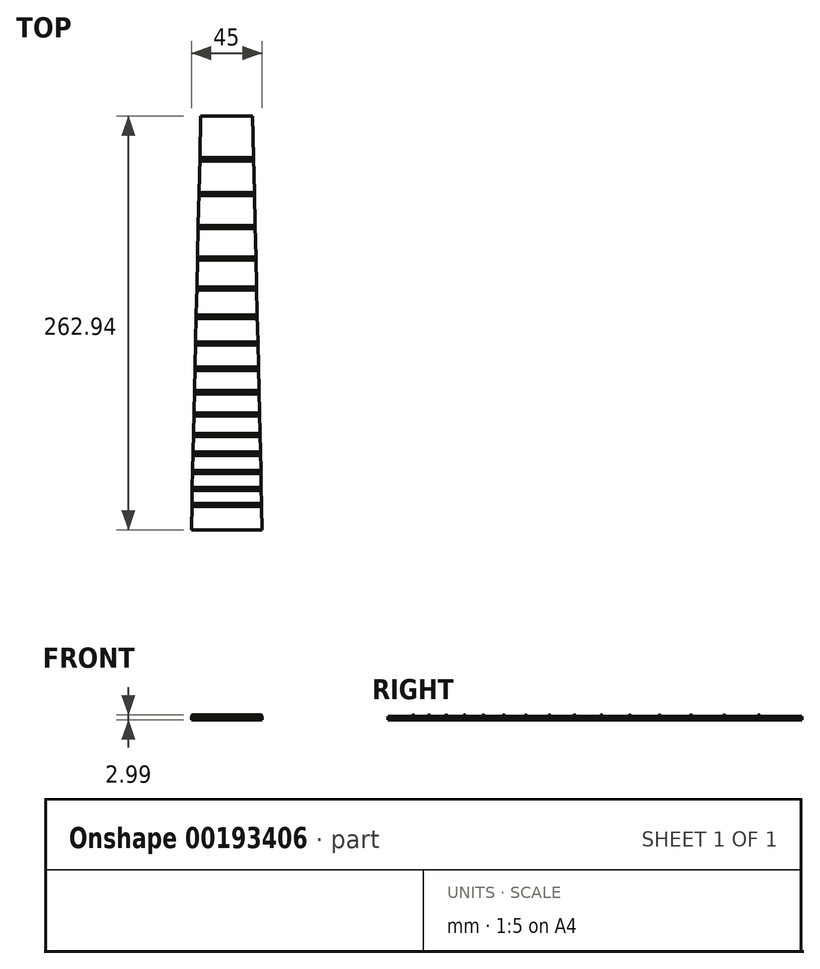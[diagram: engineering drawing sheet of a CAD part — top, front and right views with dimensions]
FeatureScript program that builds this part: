
annotation { "Feature Type Name" : "Feature", "Feature Type Description" : "" }
export const myFeature = defineFeature(function(context is Context, id is Id, definition is map)
    precondition{}
    {
        {
            var Q0;
            Q0=qCreatedBy(makeId("Top.planeOp"),FACE);
            var sketch = newSketch(context, id + "F0", { "sketchPlane" : qUnion([Q0])});
            skLineSegment(sketch, "E0", {"start": v(-15.06, 218.37) * mm, "end": v(17.94, 218.37) * mm});
            skLineSegment(sketch, "E1", {"start": v(17.94, 218.37) * mm, "end": v(23.94, -44.57) * mm});
            skLineSegment(sketch, "E2", {"start": v(23.94, -44.57) * mm, "end": v(-21.06, -44.57) * mm});
            skLineSegment(sketch, "E3", {"start": v(-21.06, -44.57) * mm, "end": v(-15.06, 218.37) * mm});
            skSolve(sketch);
        }
        {
            var Q0;
            Q0=makeQuery(id+"F0.imprint","IMPRINT",FACE,{"disambiguationData":[TD([[makeQuery(id+"F0.imprint","IMPRINT",EDGE,{"derivedFrom":sQuery(id+"F0.wireOp",EDGE,"E0")}),-1.0]])]});
            extrude(context, id + "F1", {"entities" : qUnion([Q0]), "depth" : 2 * mm});
        }
        {
            var Q0;
            Q0=makeQuery(id+"F1.opExtrude","CAP_FACE",FACE,{"disambiguationData":[OSD([sQuery(id+"F0.wireOp",EDGE,"E0"),sQuery(id+"F0.wireOp",EDGE,"E1"),sQuery(id+"F0.wireOp",EDGE,"E2"),sQuery(id+"F0.wireOp",EDGE,"E3")])],"isStart":false});
            var sketch = newSketch(context, id + "F2", { "sketchPlane" : qUnion([Q0])});
            skLineSegment(sketch, "E4.bottom", {"start": v(-20.67, -27.57) * mm, "end": v(23.6, -27.57) * mm});
            skLineSegment(sketch, "E4.top", {"start": v(-20.67, -29.57) * mm, "end": v(23.6, -29.57) * mm});
            skLineSegment(sketch, "E4.left", {"start": v(-20.67, -27.57) * mm, "end": v(-20.67, -29.57) * mm});
            skLineSegment(sketch, "E4.right", {"start": v(23.6, -27.57) * mm, "end": v(23.6, -29.57) * mm});
            skLineSegment(sketch, "E5.bottom", {"start": v(-20.44, -17.57) * mm, "end": v(23.32, -17.57) * mm});
            skLineSegment(sketch, "E5.top", {"start": v(-20.44, -19.57) * mm, "end": v(23.32, -19.57) * mm});
            skLineSegment(sketch, "E5.left", {"start": v(-20.44, -17.57) * mm, "end": v(-20.44, -19.57) * mm});
            skLineSegment(sketch, "E5.right", {"start": v(23.32, -17.57) * mm, "end": v(23.32, -19.57) * mm});
            skLineSegment(sketch, "E6.bottom", {"start": v(-20.2, -6.57) * mm, "end": v(23.07, -6.57) * mm});
            skLineSegment(sketch, "E6.top", {"start": v(-20.2, -8.57) * mm, "end": v(23.07, -8.57) * mm});
            skLineSegment(sketch, "E6.left", {"start": v(-20.2, -6.57) * mm, "end": v(-20.2, -8.57) * mm});
            skLineSegment(sketch, "E6.right", {"start": v(23.07, -6.57) * mm, "end": v(23.07, -8.57) * mm});
            skLineSegment(sketch, "E7.bottom", {"start": v(-19.93, 4.93) * mm, "end": v(22.81, 4.93) * mm});
            skLineSegment(sketch, "E7.top", {"start": v(-19.93, 2.93) * mm, "end": v(22.81, 2.93) * mm});
            skLineSegment(sketch, "E7.left", {"start": v(-19.93, 4.93) * mm, "end": v(-19.93, 2.93) * mm});
            skLineSegment(sketch, "E7.right", {"start": v(22.81, 4.93) * mm, "end": v(22.81, 2.93) * mm});
            skLineSegment(sketch, "E8.bottom", {"start": v(-19.66, 16.93) * mm, "end": v(22.54, 16.93) * mm});
            skLineSegment(sketch, "E8.top", {"start": v(-19.66, 14.93) * mm, "end": v(22.54, 14.93) * mm});
            skLineSegment(sketch, "E8.left", {"start": v(-19.66, 16.93) * mm, "end": v(-19.66, 14.93) * mm});
            skLineSegment(sketch, "E8.right", {"start": v(22.54, 16.93) * mm, "end": v(22.54, 14.93) * mm});
            skLineSegment(sketch, "E9.bottom", {"start": v(-19.36, 29.93) * mm, "end": v(22.24, 29.93) * mm});
            skLineSegment(sketch, "E9.top", {"start": v(-19.36, 27.93) * mm, "end": v(22.24, 27.93) * mm});
            skLineSegment(sketch, "E9.left", {"start": v(-19.36, 29.93) * mm, "end": v(-19.36, 27.93) * mm});
            skLineSegment(sketch, "E9.right", {"start": v(22.24, 29.93) * mm, "end": v(22.24, 27.93) * mm});
            skLineSegment(sketch, "E10.bottom", {"start": v(-19.04, 43.93) * mm, "end": v(21.92, 43.93) * mm});
            skLineSegment(sketch, "E10.top", {"start": v(-19.04, 41.93) * mm, "end": v(21.92, 41.93) * mm});
            skLineSegment(sketch, "E10.left", {"start": v(-19.04, 43.93) * mm, "end": v(-19.04, 41.93) * mm});
            skLineSegment(sketch, "E10.right", {"start": v(21.92, 43.93) * mm, "end": v(21.92, 41.93) * mm});
            skLineSegment(sketch, "E11.bottom", {"start": v(-18.7, 58.93) * mm, "end": v(21.58, 58.93) * mm});
            skLineSegment(sketch, "E11.top", {"start": v(-18.7, 56.93) * mm, "end": v(21.58, 56.93) * mm});
            skLineSegment(sketch, "E11.left", {"start": v(-18.7, 58.93) * mm, "end": v(-18.7, 56.93) * mm});
            skLineSegment(sketch, "E11.right", {"start": v(21.58, 58.93) * mm, "end": v(21.58, 56.93) * mm});
            skLineSegment(sketch, "E12.bottom", {"start": v(-18.33, 74.93) * mm, "end": v(21.21, 74.93) * mm});
            skLineSegment(sketch, "E12.top", {"start": v(-18.33, 72.93) * mm, "end": v(21.21, 72.93) * mm});
            skLineSegment(sketch, "E12.left", {"start": v(-18.33, 74.93) * mm, "end": v(-18.33, 72.93) * mm});
            skLineSegment(sketch, "E12.right", {"start": v(21.21, 74.93) * mm, "end": v(21.21, 72.93) * mm});
            skLineSegment(sketch, "E13.bottom", {"start": v(-17.94, 91.93) * mm, "end": v(20.83, 91.93) * mm});
            skLineSegment(sketch, "E13.top", {"start": v(-17.94, 89.93) * mm, "end": v(20.83, 89.93) * mm});
            skLineSegment(sketch, "E13.left", {"start": v(-17.94, 91.93) * mm, "end": v(-17.94, 89.93) * mm});
            skLineSegment(sketch, "E13.right", {"start": v(20.83, 91.93) * mm, "end": v(20.83, 89.93) * mm});
            skLineSegment(sketch, "E14.bottom", {"start": v(-17.53, 109.93) * mm, "end": v(20.41, 109.93) * mm});
            skLineSegment(sketch, "E14.top", {"start": v(-17.53, 107.93) * mm, "end": v(20.41, 107.93) * mm});
            skLineSegment(sketch, "E14.left", {"start": v(-17.53, 109.93) * mm, "end": v(-17.53, 107.93) * mm});
            skLineSegment(sketch, "E14.right", {"start": v(20.41, 109.93) * mm, "end": v(20.41, 107.93) * mm});
            skLineSegment(sketch, "E15.bottom", {"start": v(-17.1, 128.93) * mm, "end": v(19.98, 128.93) * mm});
            skLineSegment(sketch, "E15.top", {"start": v(-17.1, 126.93) * mm, "end": v(19.98, 126.93) * mm});
            skLineSegment(sketch, "E15.left", {"start": v(-17.1, 128.93) * mm, "end": v(-17.1, 126.93) * mm});
            skLineSegment(sketch, "E15.right", {"start": v(19.98, 128.93) * mm, "end": v(19.98, 126.93) * mm});
            skLineSegment(sketch, "E16.bottom", {"start": v(-16.64, 148.93) * mm, "end": v(19.52, 148.93) * mm});
            skLineSegment(sketch, "E16.top", {"start": v(-16.64, 146.93) * mm, "end": v(19.52, 146.93) * mm});
            skLineSegment(sketch, "E16.left", {"start": v(-16.64, 148.93) * mm, "end": v(-16.64, 146.93) * mm});
            skLineSegment(sketch, "E16.right", {"start": v(19.52, 148.93) * mm, "end": v(19.52, 146.93) * mm});
            skLineSegment(sketch, "E17.bottom", {"start": v(-16.16, 169.93) * mm, "end": v(19.05, 169.93) * mm});
            skLineSegment(sketch, "E17.top", {"start": v(-16.16, 167.93) * mm, "end": v(19.05, 167.93) * mm});
            skLineSegment(sketch, "E17.left", {"start": v(-16.16, 169.93) * mm, "end": v(-16.16, 167.93) * mm});
            skLineSegment(sketch, "E17.right", {"start": v(19.05, 169.93) * mm, "end": v(19.05, 167.93) * mm});
            skLineSegment(sketch, "E18.bottom", {"start": v(-15.66, 191.93) * mm, "end": v(18.54, 191.93) * mm});
            skLineSegment(sketch, "E18.top", {"start": v(-15.66, 189.93) * mm, "end": v(18.54, 189.93) * mm});
            skLineSegment(sketch, "E18.left", {"start": v(-15.66, 191.93) * mm, "end": v(-15.66, 189.93) * mm});
            skLineSegment(sketch, "E18.right", {"start": v(18.54, 191.93) * mm, "end": v(18.54, 189.93) * mm});
            skSolve(sketch);
        }
        {
            var Q0;
            Q0=qSketchRegion(id+"F2",true);
            extrude(context, id + "F3", {"entities" : qUnion([Q0]), "operationType" : NewBodyOperationType.ADD, "depth" : 1 * mm});
        }
        {
            var Q0;
            Q0=makeQuery(id+"F3.opExtrude","CAP_EDGE",EDGE,{"disambiguationData":[OSD([sQuery(id+"F2.wireOp",EDGE,"E4.top")])],"isStart":false});
            var Q1;
            Q1=makeQuery(id+"F3.opExtrude","CAP_EDGE",EDGE,{"disambiguationData":[OSD([sQuery(id+"F2.wireOp",EDGE,"E4.bottom")])],"isStart":false});
            var Q2;
            Q2=makeQuery(id+"F3.opExtrude","CAP_EDGE",EDGE,{"disambiguationData":[OSD([sQuery(id+"F2.wireOp",EDGE,"E5.top")])],"isStart":false});
            var Q3;
            Q3=makeQuery(id+"F3.opExtrude","CAP_EDGE",EDGE,{"disambiguationData":[OSD([sQuery(id+"F2.wireOp",EDGE,"E5.bottom")])],"isStart":false});
            var Q4;
            Q4=makeQuery(id+"F3.opExtrude","CAP_EDGE",EDGE,{"disambiguationData":[OSD([sQuery(id+"F2.wireOp",EDGE,"E6.top")])],"isStart":false});
            var Q5;
            Q5=makeQuery(id+"F3.opExtrude","CAP_EDGE",EDGE,{"disambiguationData":[OSD([sQuery(id+"F2.wireOp",EDGE,"E6.bottom")])],"isStart":false});
            var Q6;
            Q6=makeQuery(id+"F3.opExtrude","CAP_EDGE",EDGE,{"disambiguationData":[OSD([sQuery(id+"F2.wireOp",EDGE,"E7.top")])],"isStart":false});
            var Q7;
            Q7=makeQuery(id+"F3.opExtrude","CAP_EDGE",EDGE,{"disambiguationData":[OSD([sQuery(id+"F2.wireOp",EDGE,"E7.bottom")])],"isStart":false});
            var Q8;
            Q8=makeQuery(id+"F3.opExtrude","CAP_EDGE",EDGE,{"disambiguationData":[OSD([sQuery(id+"F2.wireOp",EDGE,"E8.top")])],"isStart":false});
            var Q9;
            Q9=makeQuery(id+"F3.opExtrude","CAP_EDGE",EDGE,{"disambiguationData":[OSD([sQuery(id+"F2.wireOp",EDGE,"E8.bottom")])],"isStart":false});
            var Q10;
            Q10=makeQuery(id+"F3.opExtrude","CAP_EDGE",EDGE,{"disambiguationData":[OSD([sQuery(id+"F2.wireOp",EDGE,"E9.top")])],"isStart":false});
            var Q11;
            Q11=makeQuery(id+"F3.opExtrude","CAP_EDGE",EDGE,{"disambiguationData":[OSD([sQuery(id+"F2.wireOp",EDGE,"E9.bottom")])],"isStart":false});
            var Q12;
            Q12=makeQuery(id+"F3.opExtrude","CAP_EDGE",EDGE,{"disambiguationData":[OSD([sQuery(id+"F2.wireOp",EDGE,"E10.top")])],"isStart":false});
            var Q13;
            Q13=makeQuery(id+"F3.opExtrude","CAP_EDGE",EDGE,{"disambiguationData":[OSD([sQuery(id+"F2.wireOp",EDGE,"E10.bottom")])],"isStart":false});
            var Q14;
            Q14=makeQuery(id+"F3.opExtrude","CAP_EDGE",EDGE,{"disambiguationData":[OSD([sQuery(id+"F2.wireOp",EDGE,"E11.top")])],"isStart":false});
            var Q15;
            Q15=makeQuery(id+"F3.opExtrude","CAP_EDGE",EDGE,{"disambiguationData":[OSD([sQuery(id+"F2.wireOp",EDGE,"E11.bottom")])],"isStart":false});
            var Q16;
            Q16=makeQuery(id+"F3.opExtrude","CAP_EDGE",EDGE,{"disambiguationData":[OSD([sQuery(id+"F2.wireOp",EDGE,"E12.top")])],"isStart":false});
            var Q17;
            Q17=makeQuery(id+"F3.opExtrude","CAP_EDGE",EDGE,{"disambiguationData":[OSD([sQuery(id+"F2.wireOp",EDGE,"E12.bottom")])],"isStart":false});
            var Q18;
            Q18=makeQuery(id+"F3.opExtrude","CAP_EDGE",EDGE,{"disambiguationData":[OSD([sQuery(id+"F2.wireOp",EDGE,"E13.top")])],"isStart":false});
            var Q19;
            Q19=makeQuery(id+"F3.opExtrude","CAP_EDGE",EDGE,{"disambiguationData":[OSD([sQuery(id+"F2.wireOp",EDGE,"E13.bottom")])],"isStart":false});
            var Q20;
            Q20=makeQuery(id+"F3.opExtrude","CAP_EDGE",EDGE,{"disambiguationData":[OSD([sQuery(id+"F2.wireOp",EDGE,"E14.top")])],"isStart":false});
            var Q21;
            Q21=makeQuery(id+"F3.opExtrude","CAP_EDGE",EDGE,{"disambiguationData":[OSD([sQuery(id+"F2.wireOp",EDGE,"E14.bottom")])],"isStart":false});
            var Q22;
            Q22=makeQuery(id+"F3.opExtrude","CAP_EDGE",EDGE,{"disambiguationData":[OSD([sQuery(id+"F2.wireOp",EDGE,"E15.top")])],"isStart":false});
            var Q23;
            Q23=makeQuery(id+"F3.opExtrude","CAP_EDGE",EDGE,{"disambiguationData":[OSD([sQuery(id+"F2.wireOp",EDGE,"E15.bottom")])],"isStart":false});
            var Q24;
            Q24=makeQuery(id+"F3.opExtrude","CAP_EDGE",EDGE,{"disambiguationData":[OSD([sQuery(id+"F2.wireOp",EDGE,"E16.top")])],"isStart":false});
            var Q25;
            Q25=makeQuery(id+"F3.opExtrude","CAP_EDGE",EDGE,{"disambiguationData":[OSD([sQuery(id+"F2.wireOp",EDGE,"E16.bottom")])],"isStart":false});
            var Q26;
            Q26=makeQuery(id+"F3.opExtrude","CAP_EDGE",EDGE,{"disambiguationData":[OSD([sQuery(id+"F2.wireOp",EDGE,"E17.top")])],"isStart":false});
            var Q27;
            Q27=makeQuery(id+"F3.opExtrude","CAP_EDGE",EDGE,{"disambiguationData":[OSD([sQuery(id+"F2.wireOp",EDGE,"E17.bottom")])],"isStart":false});
            var Q28;
            Q28=makeQuery(id+"F3.opExtrude","CAP_EDGE",EDGE,{"disambiguationData":[OSD([sQuery(id+"F2.wireOp",EDGE,"E18.top")])],"isStart":false});
            var Q29;
            Q29=makeQuery(id+"F3.opExtrude","CAP_EDGE",EDGE,{"disambiguationData":[OSD([sQuery(id+"F2.wireOp",EDGE,"E18.bottom")])],"isStart":false});
            fillet(context, id + "F4", {"entities" : qUnion([Q0, Q1, Q2, Q3, Q4, Q5, Q6, Q7, Q8, Q9, Q10, Q11, Q12, Q13, Q14, Q15, Q16, Q17, Q18, Q19, Q20, Q21, Q22, Q23, Q24, Q25, Q26, Q27, Q28, Q29]), "radius" : 1.2 * mm, "tangentPropagation" : true, "allowEdgeOverflow" : false});
        }
    });
